FCSTD DOCUMENT  (FreeCAD 1.0R39319 (Git))
Label: Modul_zahnkonstrtion_v2
License: All rights reserved
LicenseURL: http://en.wikipedia.org/wiki/All_rights_reserved
objects: Sketcher::SketchObject×1, PartDesign::Body×1, Spreadsheet::Sheet×1
note: 3 computed .brp shape members not serialized (recipe doc carries the construction recipe); baked Part::Feature solids carry a one-line shape summary decoded from their .brp

FEATURE [Sketcher::SketchObject] Sketch
  ArcFitTolerance = 1e-06
  AttachmentSupport = -> [XY_Plane]
  FullyConstrained = true
  MakeInternals = false
  MapMode = 5
  expr: Constraints[10] = <<tabelle>>.Ha
  expr: Constraints[11] = pi / 2 * <<tabelle>>.modul
  expr: Constraints[12] = <<tabelle>>.Hf
  expr: Constraints[14] = <<tabelle>>.L_constr * <<tabelle>>.Step
  expr: Constraints[18] = <<tabelle>>.modul + <<tabelle>>.D / 2
  expr: Constraints[23] = <<tabelle>>.D / 2 + <<tabelle>>.Hf
  expr: Constraints[24] = <<tabelle>>.D / 2 - <<tabelle>>.Hf
  expr: Constraints[26] = <<tabelle>>.D / 2
  expr: Constraints[27] = <<tabelle>>.W_constr * <<tabelle>>.Step
  sketch-geometry (14):
    g0: LineSegment [constr] StartX=0 StartY=0.622566 StartZ=0 EndX=2.16667 EndY=1.41117 EndZ=0
    g1: LineSegment [constr] StartX=2.16667 StartY=1.41117 StartZ=0 EndX=2.16667 EndY=2.25402 EndZ=0
    g2: LineSegment [constr] StartX=2.16667 StartY=2.25402 StartZ=0 EndX=0 EndY=3.04263 EndZ=0
    g3: LineSegment [constr] StartX=1.16667 StartY=1.0472 StartZ=0 EndX=1.16667 EndY=2.61799 EndZ=0
    g4: GeomPoint [constr] X=2.16667 Y=1.8326 Z=0
    g5: LineSegment [constr] StartX=2.16667 StartY=1.41117 StartZ=0 EndX=2.16667 EndY=0 EndZ=0
    g6: ArcOfCircle [constr] CenterX=16.1667 CenterY=0 CenterZ=0 NormalX=0 NormalY=0 NormalZ=1 AngleXU=0 Radius=16 StartAngle=1.5708 EndAngle=3.14159
    g7: LineSegment [constr] StartX=1.16667 StartY=0 StartZ=0 EndX=1.16667 EndY=2.61799 EndZ=0
    g8: ArcOfCircle [constr] CenterX=16.1667 CenterY=0 CenterZ=0 NormalX=0 NormalY=0 NormalZ=1 AngleXU=0 Radius=13.8333 StartAngle=1.5708 EndAngle=3.14159
    g9: LineSegment StartX=16.1667 StartY=0 StartZ=0 EndX=1.20321 EndY=1.04635 EndZ=0
    g10: LineSegment StartX=1.20321 StartY=1.04635 StartZ=0 EndX=1.15948 EndY=1.03381 EndZ=0
    g11: LineSegment StartX=1.20321 StartY=1.04635 StartZ=0 EndX=1.25025 EndY=1.05984 EndZ=0
    g12: LineSegment StartX=1.15948 StartY=1.03381 StartZ=0 EndX=1.06974 EndY=1.00637 EndZ=0
    g13: LineSegment StartX=1.06974 StartY=1.00637 StartZ=0 EndX=0.976417 EndY=0.97605 EndZ=0
  constraints (45):
    c: PointOnObject(g0,g-2)
    c: Coincident(g0,g1)
    c: Coincident(g1,g2)
    c: PointOnObject(g2,g-2)
    c: Vertical(g1)
    c: Angle(g1,g0) = 1.91986
    c: Angle(g2,g1) = 1.91986
    c: PointOnObject(g3,g0)
    c: PointOnObject(g3,g2)
    c: Vertical(g3)
    c: DistanceX(g3,g0) = 1
    c: Distance(g3) = 1.5708
    c: DistanceX(g2,g3) = 1.16667
    c: Symmetric(g0,g1,g4)
    c: DistanceY(g-1,g3) = 1.0472
    c: Coincident(g0,g5)
    c: Vertical(g5)
    c: PointOnObject(g6,g-1)
    c: Radius(g6) = 16
    c: PointOnObject(g7,g-1)
    c: Vertical(g7)
    c: PointOnObject(g8,g-1)
    c: PointOnObject(g6,g-1)
    c: Distance(g-1,g6) = 16.1667
    c: Radius(g8) = 13.8333
    c: Coincident(g7,g3)
    c: Distance(g9) = 15
    c: Angle(g9,g-1) = 0.0698132
    c: PointOnObject(g5,g-1)
    c: Vertical(g8,g6)
    c: Vertical(g6,g6)
    c: Coincident(g9,g10)
    c: Angle(g10,g9) = 2.79253
    c: Coincident(g9,g11)
    c: Distance(g10) = 0.045487
    c: Angle(g9,g11) = 0.349066
    c: Coincident(g10,g12)
    c: Angle(g12,g10) = 3.12414
    c: Distance(g12) = 0.093837
    c: Distance(g11) = 0.048941
    c: Coincident(g12,g13)
    c: Angle(g13,g12) = 3.12414
    c: Distance(g13) = 0.09813
    c: Coincident(g8,g9)
    c: Coincident(g8,g6)
FEATURE [PartDesign::Body] Body  label="Körper"
  AllowCompound = false
  Group = -> [Sketch]
  Origin = -> Origin
FEATURE [Spreadsheet::Sheet] Spreadsheet  label="tabelle"
  cells = A1='m; B1(modul)=1; C1='Modul; D1='ISO-Modul; A2='z; B2(zaehhnezal)=30; C2='Zänezahl; D2='count teeth; A3='Ha; B3(Ha)==modul; C3='Zahnhöhe Mitte bis Kopf = Modul m; D3='tooth hight from middle to tooth tip, addendum Ha = m; A4='c; B4(c)==modul / 6; C4='Zahnkopfluft c = m / 6; D4='tooth tip space, clearance c = ISO-Modul / 6; A5='Hf; B5(Hf)==c + modul; C5='Zahntiefe Mitte bis Boden, Hf = Ha + c; D5='tooth depth rom middle to tooth base dedendum,, Hf = Ha + c; A6='D; B6(D)==zaehhnezal * modul; C6='Teil-Kreis-Durchmesser D = m * z , nur für Zanräder mit z = Zähnezahl; D6='pich diameter, parted circle diameter, D = m  * z; A7='Da; B7(Da)==D + 2 * modul; C7=' Durchmesser_außen, Da = D + 2 * modul; D7='adenim diameter, Da = D + 2 * modul; A9='W_constr; B9(W_constr)=1; C9='Konstrktionswinkel / Schritt in [°]; D9='constrction angle / step in [°]; A10='L_constr; B10(L_constr)==D * pi / 360 * W_constr; C10='Delta Zahnstangenverschiebung / Step = D * pi / 360° * W_constr; D10='delta shift of the cutting tool, toothbar per step,  = D * pi / 360° * W_constr; A11='Step; B11(Step)=4; D11='step number; A12='W_linien; B12(W_linien)==180 - W_constr; C12='Winkel von Linie zu Linie = 180 - W_constr; D12='angel from line to line  = 180 - W_constr; B13='`160 °; C13='Erster Winkel zur Radiuslinie = 180° - Flankenwinkel des Modulfräsers; D13='firsst angle to the radius line = 180° - flank angle of the ISO-Modul milling cutter
